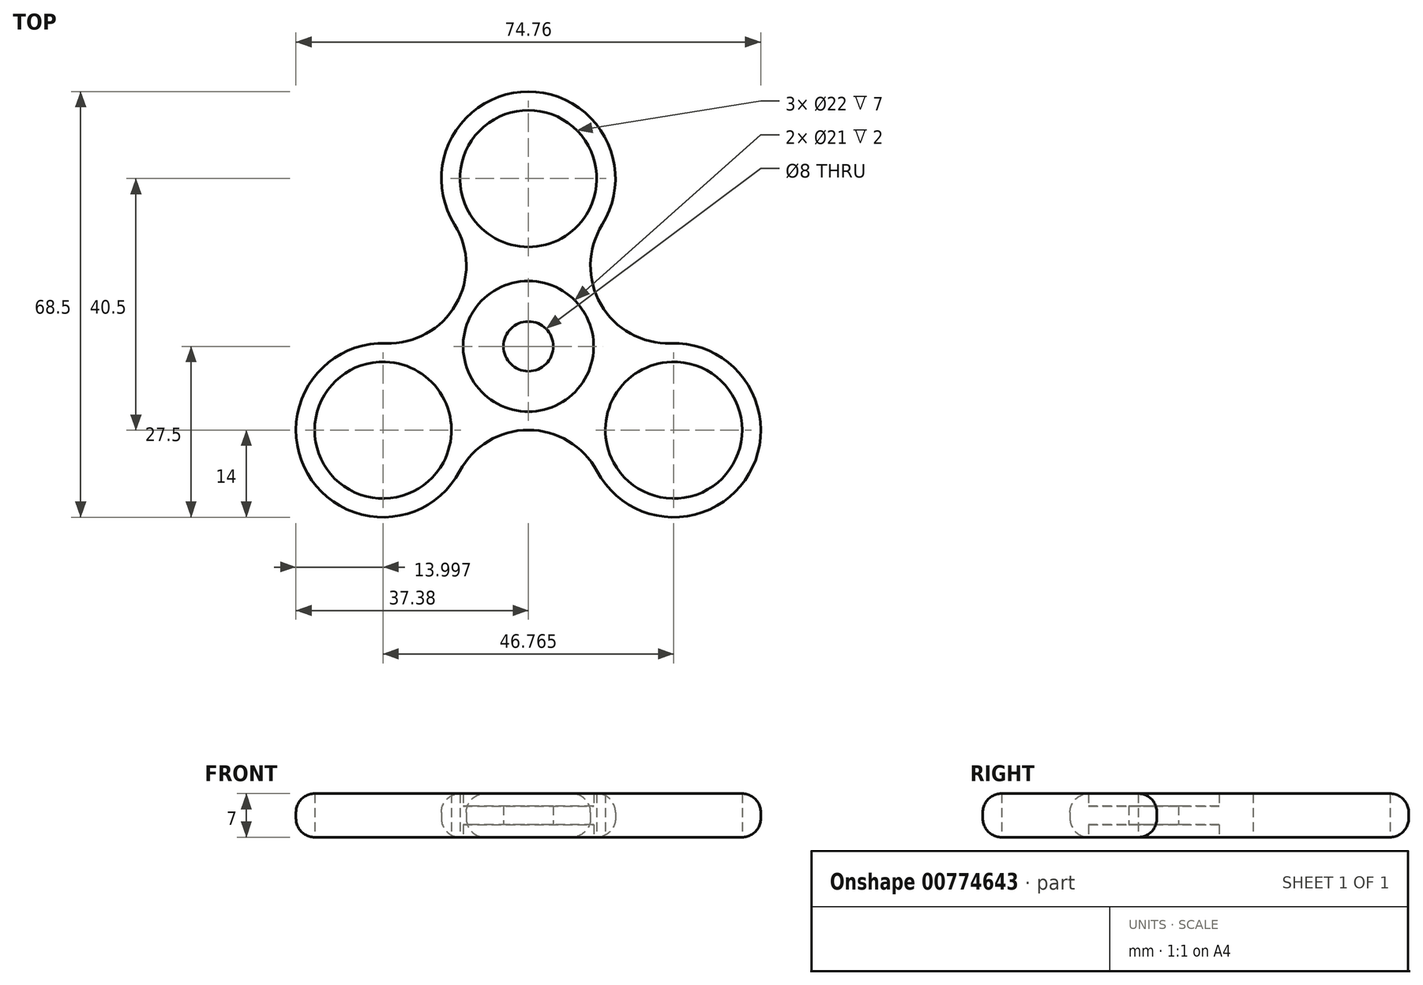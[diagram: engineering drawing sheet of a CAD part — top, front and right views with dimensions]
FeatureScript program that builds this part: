
annotation { "Feature Type Name" : "Feature", "Feature Type Description" : "" }
export const myFeature = defineFeature(function(context is Context, id is Id, definition is map)
    precondition{}
    {
        {
            var Q0;
            Q0=qCreatedBy(makeId("Top.planeOp"),FACE);
            var sketch = newSketch(context, id + "F0", { "sketchPlane" : qUnion([Q0])});
            skCircle(sketch, "E0", {"center": v(0, 0) * mm, "radius": 4 * mm});
            skCircle(sketch, "E1", {"center": v(0, 27) * mm, "radius": 11 * mm});
            skLineSegment(sketch, "E2", {"start": v(0, 0) * mm, "end": v(0, 27) * mm});
            skCircle(sketch, "E3", {"center": v(-23.38, -13.5) * mm, "radius": 11 * mm});
            skCircle(sketch, "E4", {"center": v(23.38, -13.5) * mm, "radius": 11 * mm});
            skArc(sketch, "E5", {"start": v(-22.91, 0.5) * mm, "mid": v(-11.67, 6.73) * mm, "end": v(-11.88, 19.6) * mm});
            skArc(sketch, "E6.1.0", {"start": v(11.03, -20.09) * mm, "mid": v(0, -13.47) * mm, "end": v(-11.03, -20.09) * mm});
            skArc(sketch, "E6.2.0", {"start": v(11.88, 19.6) * mm, "mid": v(11.67, 6.73) * mm, "end": v(22.91, 0.5) * mm});
            skArc(sketch, "E7", {"start": v(-22.91, 0.5) * mm, "mid": v(-35.5, -20.5) * mm, "end": v(-11.03, -20.09) * mm});
            skArc(sketch, "E8", {"start": v(11.88, 19.6) * mm, "mid": v(0, 41) * mm, "end": v(-11.88, 19.6) * mm});
            skArc(sketch, "E9", {"start": v(11.03, -20.09) * mm, "mid": v(35.5, -20.5) * mm, "end": v(22.91, 0.5) * mm});
            skCircle(sketch, "E10", {"center": v(0, 0) * mm, "radius": 13.5 * mm});
            skCircle(sketch, "E11", {"center": v(0, 0) * mm, "radius": 10.5 * mm});
            skSolve(sketch);
        }
        {
            var Q0;
            Q0=makeQuery(id+"F0.imprint","IMPRINT",FACE,{"disambiguationData":[TD([[makeQuery(id+"F0.imprint","IMPRINT",EDGE,{"derivedFrom":sQuery(id+"F0.wireOp",EDGE,"E4")}),-1.0]])]});
            var Q1;
            Q1=makeQuery(id+"F0.imprint","IMPRINT",FACE,{"disambiguationData":[TD([[makeQuery(id+"F0.imprint","IMPRINT",EDGE,{"derivedFrom":sQuery(id+"F0.wireOp",EDGE,"E3")}),-1.0]])]});
            var Q2;
            Q2=makeQuery(id+"F0.imprint","IMPRINT",FACE,{"disambiguationData":[TD([[makeQuery(id+"F0.imprint","IMPRINT",EDGE,{"derivedFrom":sQuery(id+"F0.wireOp",EDGE,"E1")}),-1.0]])]});
            var Q3;
            Q3=makeQuery(id+"F0.imprint","IMPRINT",FACE,{"disambiguationData":[TD([[makeQuery(id+"F0.imprint","IMPRINT",EDGE,{"derivedFrom":sQuery(id+"F0.wireOp",EDGE,"E11")}),-1.0]])]});
            extrude(context, id + "F1", {"entities" : qUnion([Q0, Q1, Q2, Q3]), "endBound" : BoundingType.SYMMETRIC, "depth" : 7 * mm, "offsetDistance" : 25 * mm});
        }
        {
            var Q0;
            Q0=makeQuery(id+"F1.opExtrude","CAP_EDGE",EDGE,{"disambiguationData":[OSD([sQuery(id+"F0.wireOp",EDGE,"E6.1.0")])],"isStart":false});
            var Q1;
            Q1=makeQuery(id+"F1.opExtrude","SWEPT_FACE",FACE,{"disambiguationData":[OSD([sQuery(id+"F0.wireOp",EDGE,"E6.1.0")])]});
            fillet(context, id + "F2", {"entities" : qUnion([Q0, Q1]), "radius" : 3 * mm, "tangentPropagation" : true, "allowEdgeOverflow" : false});
        }
        {
            var Q0;
            Q0=makeQuery(id+"F0.imprint","IMPRINT",FACE,{"disambiguationData":[TD([[makeQuery(id+"F0.imprint","IMPRINT",EDGE,{"derivedFrom":sQuery(id+"F0.wireOp",EDGE,"E0")}),-1.0]])]});
            extrude(context, id + "F3", {"entities" : qUnion([Q0]), "operationType" : NewBodyOperationType.ADD, "endBound" : BoundingType.SYMMETRIC, "depth" : 3 * mm, "offsetDistance" : 25 * mm});
        }
    });
